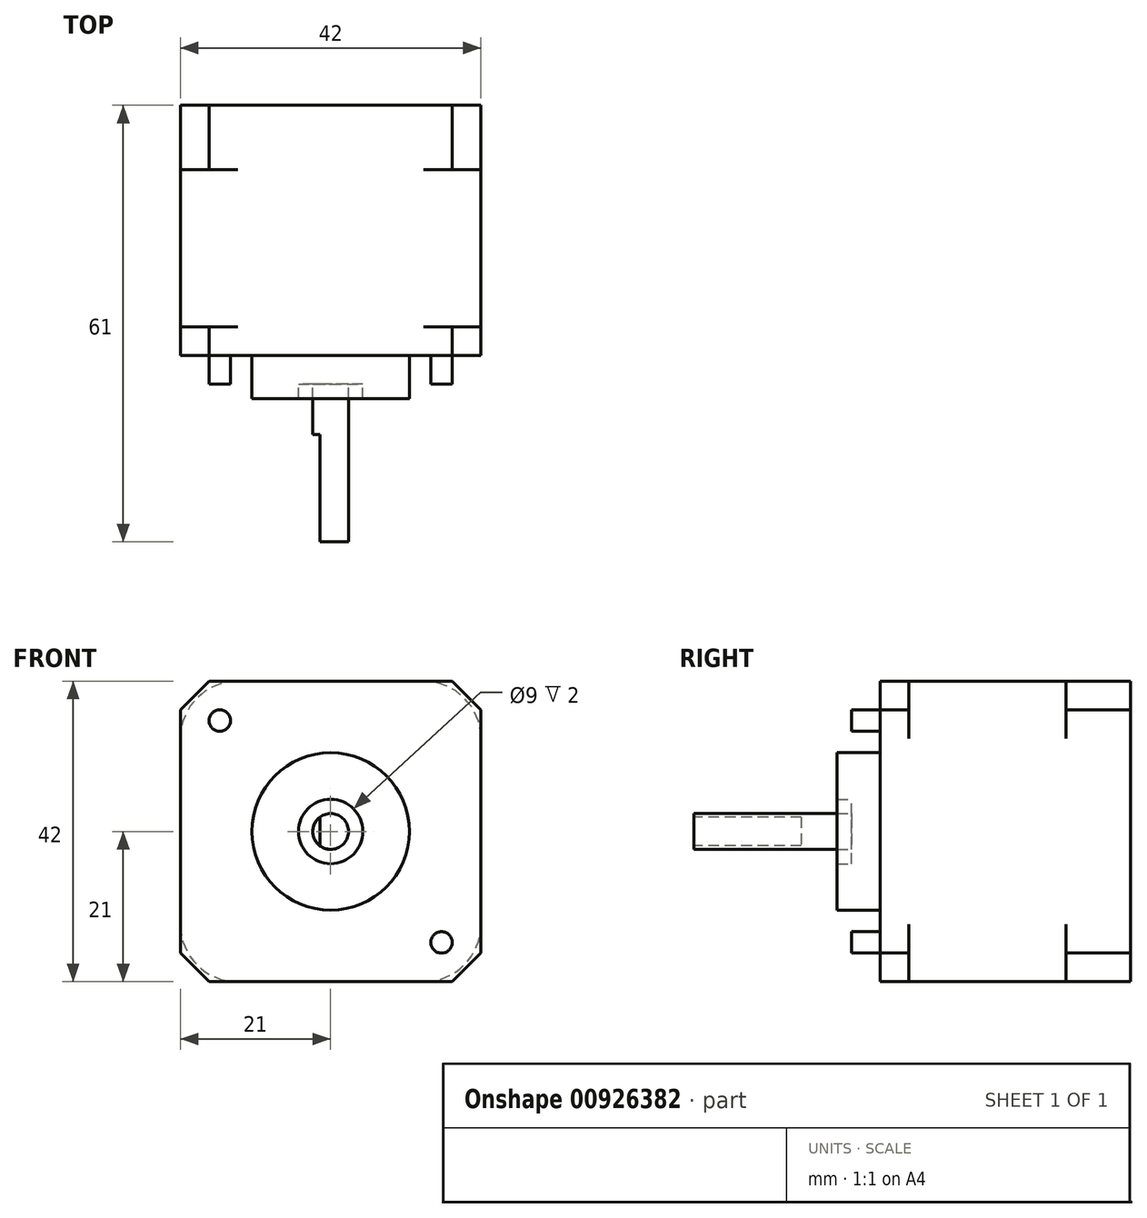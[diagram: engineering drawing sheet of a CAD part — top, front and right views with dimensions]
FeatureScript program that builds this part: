
annotation { "Feature Type Name" : "Feature", "Feature Type Description" : "" }
export const myFeature = defineFeature(function(context is Context, id is Id, definition is map)
    precondition{}
    {
        {
            var Q0;
            Q0=qCreatedBy(makeId("Front.planeOp"),FACE);
            var sketch = newSketch(context, id + "F0", { "sketchPlane" : qUnion([Q0])});
            skLineSegment(sketch, "E0.bottom", {"start": v(0, 0) * mm, "end": v(42, 0) * mm});
            skLineSegment(sketch, "E0.top", {"start": v(0, 42) * mm, "end": v(42, 42) * mm});
            skLineSegment(sketch, "E0.left", {"start": v(0, 0) * mm, "end": v(0, 42) * mm});
            skLineSegment(sketch, "E0.right", {"start": v(42, 0) * mm, "end": v(42, 42) * mm});
            skSolve(sketch);
        }
        {
            var Q0;
            Q0 = qSketchRegion(id + "F0", true);
            extrude(context, id + "F1", {"entities" : qUnion([Q0]), "depth" : 8 * mm, "offsetDistance" : 25 * mm});
        }
        {
            var Q0;
            Q0=makeQuery(id+"F1.opExtrude","CAP_FACE",FACE,{"disambiguationData":[OSD([sQuery(id+"F0.wireOp",EDGE,"E0.bottom"),sQuery(id+"F0.wireOp",EDGE,"E0.top"),sQuery(id+"F0.wireOp",EDGE,"E0.left"),sQuery(id+"F0.wireOp",EDGE,"E0.right")])],"isStart":true});
            var sketch = newSketch(context, id + "F2", { "sketchPlane" : qUnion([Q0])});
            skLineSegment(sketch, "E1", {"start": v(0, 21) * mm, "end": v(-42, 21) * mm, "construction": true});
            skLineSegment(sketch, "E2", {"start": v(-21, 42) * mm, "end": v(-21, 0) * mm, "construction": true});
            skLineSegment(sketch, "E3", {"start": v(0, 21) * mm, "end": v(0, 34) * mm});
            skLineSegment(sketch, "E4", {"start": v(-8, 42) * mm, "end": v(-21, 42) * mm});
            skLineSegment(sketch, "E5.MirrorCS", {"start": v(0, 21) * mm, "end": v(0, 8) * mm});
            skLineSegment(sketch, "E6.MirrorCS", {"start": v(-8, 0) * mm, "end": v(-21, 0) * mm});
            skLineSegment(sketch, "E7.MirrorCS", {"start": v(-42, 21) * mm, "end": v(-42, 8) * mm});
            skLineSegment(sketch, "E8.MirrorCS", {"start": v(-34, 42) * mm, "end": v(-21, 42) * mm});
            skLineSegment(sketch, "E9.MirrorCS", {"start": v(-34, 0) * mm, "end": v(-21, 0) * mm});
            skLineSegment(sketch, "E10.MirrorCS", {"start": v(-42, 21) * mm, "end": v(-42, 34) * mm});
            skArc(sketch, "E11", {"start": v(0, 34) * mm, "mid": v(-2.34, 39.66) * mm, "end": v(-8, 42) * mm});
            skArc(sketch, "E12.MirrorCS", {"start": v(0, 8) * mm, "mid": v(-2.34, 2.34) * mm, "end": v(-8, 0) * mm});
            skArc(sketch, "E13.MirrorCS", {"start": v(-42, 34) * mm, "mid": v(-39.66, 39.66) * mm, "end": v(-34, 42) * mm});
            skArc(sketch, "E14.MirrorCS", {"start": v(-42, 8) * mm, "mid": v(-39.66, 2.34) * mm, "end": v(-34, 0) * mm});
            skSolve(sketch);
        }
        {
            var Q0;
            Q0 = qSketchRegion(id + "F2", true);
            extrude(context, id + "F3", {"entities" : qUnion([Q0]), "operationType" : NewBodyOperationType.ADD, "depth" : 22 * mm, "offsetDistance" : 25 * mm});
        }
        {
            var Q0;
            Q0=makeQuery(id+"F3.opExtrude","CAP_FACE",FACE,{"disambiguationData":[OSD([sQuery(id+"F2.wireOp",EDGE,"E3"),sQuery(id+"F2.wireOp",EDGE,"TS49GkIp-gIQR-fzWl-7jLC-N3Z3hN07Um4u"),sQuery(id+"F2.wireOp",EDGE,"E4"),sQuery(id+"F2.wireOp",EDGE,"E5.MirrorCS"),sQuery(id+"F2.wireOp",EDGE,"e7304309-2cf8-4616-bcc9-8bdb39e604d01.MirrorCS"),sQuery(id+"F2.wireOp",EDGE,"E6.MirrorCS"),sQuery(id+"F2.wireOp",EDGE,"E7.MirrorCS"),sQuery(id+"F2.wireOp",EDGE,"8c1482cd-ad9f-4f6b-a8f8-884175ea14cf1.MirrorCS"),sQuery(id+"F2.wireOp",EDGE,"E8.MirrorCS"),sQuery(id+"F2.wireOp",EDGE,"8c1482cd-ad9f-4f6b-a8f8-884175ea14cf3.MirrorCS"),sQuery(id+"F2.wireOp",EDGE,"E9.MirrorCS"),sQuery(id+"F2.wireOp",EDGE,"E10.MirrorCS")])],"isStart":false});
            var sketch = newSketch(context, id + "F4", { "sketchPlane" : qUnion([Q0])});
            skLineSegment(sketch, "E15.bottom", {"start": v(0, 0) * mm, "end": v(-42, 0) * mm});
            skLineSegment(sketch, "E15.top", {"start": v(0, 42) * mm, "end": v(-42, 42) * mm});
            skLineSegment(sketch, "E15.left", {"start": v(0, 0) * mm, "end": v(0, 42) * mm});
            skLineSegment(sketch, "E15.right", {"start": v(-42, 0) * mm, "end": v(-42, 42) * mm});
            skSolve(sketch);
        }
        {
            var Q0;
            Q0 = qSketchRegion(id + "F4", true);
            extrude(context, id + "F5", {"entities" : qUnion([Q0]), "operationType" : NewBodyOperationType.ADD, "depth" : 9 * mm, "offsetDistance" : 25 * mm});
        }
        {
            var Q0;
            Q0=makeQuery(id+"F1.opExtrude","CAP_FACE",FACE,{"disambiguationData":[OSD([sQuery(id+"F0.wireOp",EDGE,"E0.bottom"),sQuery(id+"F0.wireOp",EDGE,"E0.top"),sQuery(id+"F0.wireOp",EDGE,"E0.left"),sQuery(id+"F0.wireOp",EDGE,"E0.right")])],"isStart":false});
            var sketch = newSketch(context, id + "F6", { "sketchPlane" : qUnion([Q0])});
            skLineSegment(sketch, "E16", {"start": v(0, 21) * mm, "end": v(42, 21) * mm, "construction": true});
            skLineSegment(sketch, "E17", {"start": v(21, 0) * mm, "end": v(21, 42) * mm, "construction": true});
            skCircle(sketch, "E18", {"center": v(21, 21) * mm, "radius": 11 * mm});
            skCircle(sketch, "E19", {"center": v(21, 21) * mm, "radius": 4.5 * mm});
            skSolve(sketch);
        }
        {
            var Q0;
            Q0=makeQuery(id+"F6.imprint","IMPRINT",FACE,{"disambiguationData":[TD([[makeQuery(id+"F6.imprint","IMPRINT",EDGE,{"derivedFrom":sQuery(id+"F6.wireOp",EDGE,"E18")}),1.0]])]});
            extrude(context, id + "F7", {"entities" : qUnion([Q0]), "operationType" : NewBodyOperationType.ADD, "depth" : 2 * mm, "offsetDistance" : 25 * mm});
        }
        {
            var Q0;
            Q0=makeQuery(id+"F7.boolean.opBoolean","SPLIT",FACE,{"disambiguationData":[TD([makeQuery(id+"F7.opExtrude","SWEPT_FACE",FACE,{"disambiguationData":[OSD([sQuery(id+"F6.wireOp",EDGE,"E19")])]})])],"derivedFrom":makeQuery(id+"F1.opExtrude","CAP_FACE",FACE,{"disambiguationData":[OSD([sQuery(id+"F0.wireOp",EDGE,"E0.bottom"),sQuery(id+"F0.wireOp",EDGE,"E0.top"),sQuery(id+"F0.wireOp",EDGE,"E0.left"),sQuery(id+"F0.wireOp",EDGE,"E0.right")])],"isStart":false})});
            var sketch = newSketch(context, id + "F8", { "sketchPlane" : qUnion([Q0])});
            skCircle(sketch, "E20", {"center": v(21, 21) * mm, "radius": 2.5 * mm});
            skSolve(sketch);
        }
        {
            var Q0;
            Q0 = qSketchRegion(id + "F8", true);
            extrude(context, id + "F9", {"entities" : qUnion([Q0]), "operationType" : NewBodyOperationType.ADD, "depth" : 22 * mm, "offsetDistance" : 25 * mm});
        }
        {
            var Q0;
            Q0=makeQuery(id+"F9.opExtrude","CAP_FACE",FACE,{"disambiguationData":[OSD([sQuery(id+"F8.wireOp",EDGE,"E20")])],"isStart":false});
            var sketch = newSketch(context, id + "F10", { "sketchPlane" : qUnion([Q0])});
            skLineSegment(sketch, "E21.bottom", {"start": v(19.5, 23) * mm, "end": v(18.5, 23) * mm});
            skLineSegment(sketch, "E21.top", {"start": v(19.5, 19) * mm, "end": v(18.5, 19) * mm});
            skLineSegment(sketch, "E21.left", {"start": v(19.5, 23) * mm, "end": v(19.5, 19) * mm});
            skLineSegment(sketch, "E21.right", {"start": v(18.5, 23) * mm, "end": v(18.5, 19) * mm});
            skSolve(sketch);
        }
        {
            var Q0;
            {var subQ0=sQuery(id+"F10.wireOp",EDGE,"E21.left");Q0=makeQuery(id+"F10.imprint","IMPRINT",FACE,{"disambiguationData":[TD([[makeQuery(id+"F10.imprint","IMPRINT",EDGE,{"derivedFrom":subQ0}),-1.0]])]});}
            extrude(context, id + "F11", {"entities" : qUnion([Q0]), "operationType" : NewBodyOperationType.REMOVE, "oppositeDirection" : true, "depth" : 15 * mm, "offsetDistance" : 25 * mm});
        }
        {
            var Q0;
            {var subQ0=sQuery(id+"F0.wireOp",EDGE,"E0.top");var subQ1=sQuery(id+"F0.wireOp",EDGE,"E0.bottom");var subQ2=sQuery(id+"F0.wireOp",EDGE,"E0.left");var subQ3=sQuery(id+"F0.wireOp",EDGE,"E0.right");Q0=makeQuery(id+"F7.boolean.opBoolean","SPLIT",FACE,{"disambiguationData":[TD([makeQuery(id+"F1.opExtrude","SWEPT_FACE",FACE,{"disambiguationData":[OSD([subQ1])]})])],"derivedFrom":makeQuery(id+"F1.opExtrude","CAP_FACE",FACE,{"disambiguationData":[OSD([subQ1,subQ0,subQ2,subQ3])],"isStart":false})});}
            var sketch = newSketch(context, id + "F12", { "sketchPlane" : qUnion([Q0])});
            skCircle(sketch, "E22", {"center": v(5.5, 5.5) * mm, "radius": 1.5 * mm});
            skLineSegment(sketch, "E23", {"start": v(0, 21) * mm, "end": v(42, 21) * mm, "construction": true});
            skLineSegment(sketch, "E24", {"start": v(21, 0) * mm, "end": v(21, 42) * mm, "construction": true});
            skCircle(sketch, "E25.MirrorC", {"center": v(5.5, 36.5) * mm, "radius": 1.5 * mm});
            skCircle(sketch, "E26.MirrorC", {"center": v(36.5, 36.5) * mm, "radius": 1.5 * mm});
            skCircle(sketch, "E27.MirrorC", {"center": v(36.5, 5.5) * mm, "radius": 1.5 * mm});
            skSolve(sketch);
        }
        {
            var Q0;
            Q0=makeQuery(id+"F12.imprint","IMPRINT",FACE,{"disambiguationData":[TD([[makeQuery(id+"F12.imprint","IMPRINT",EDGE,{"derivedFrom":sQuery(id+"F12.wireOp",EDGE,"E22")}),1.0]])]});
            var Q1;
            Q1=makeQuery(id+"F12.imprint","IMPRINT",FACE,{"disambiguationData":[TD([[makeQuery(id+"F12.imprint","IMPRINT",EDGE,{"derivedFrom":sQuery(id+"F12.wireOp",EDGE,"E25.MirrorC")}),-1.0]])]});
            var Q2;
            Q2=makeQuery(id+"F12.imprint","IMPRINT",FACE,{"disambiguationData":[TD([[makeQuery(id+"F12.imprint","IMPRINT",EDGE,{"derivedFrom":sQuery(id+"F12.wireOp",EDGE,"E26.MirrorC")}),1.0]])]});
            var Q3;
            Q3=makeQuery(id+"F12.imprint","IMPRINT",FACE,{"disambiguationData":[TD([[makeQuery(id+"F12.imprint","IMPRINT",EDGE,{"derivedFrom":sQuery(id+"F12.wireOp",EDGE,"E27.MirrorC")}),-1.0]])]});
            extrude(context, id + "F13", {"entities" : qUnion([Q0, Q1, Q2, Q3]), "operationType" : NewBodyOperationType.REMOVE, "oppositeDirection" : true, "depth" : 4 * mm, "offsetDistance" : 25 * mm});
        }
        {
            var Q0;
            Q0=makeQuery(id+"F1.opExtrude","SWEPT_EDGE",EDGE,{"disambiguationData":[OSD([sQuery(id+"F0.wireOp",EDGE,"E0.top"),sQuery(id+"F0.wireOp",EDGE,"E0.left")])]});
            var Q1;
            Q1=makeQuery(id+"F5.opExtrude","SWEPT_EDGE",EDGE,{"disambiguationData":[OSD([sQuery(id+"F4.wireOp",EDGE,"E15.top"),sQuery(id+"F4.wireOp",EDGE,"E15.left")])]});
            var Q2;
            Q2=makeQuery(id+"F1.opExtrude","SWEPT_EDGE",EDGE,{"disambiguationData":[OSD([sQuery(id+"F0.wireOp",EDGE,"E0.top"),sQuery(id+"F0.wireOp",EDGE,"E0.right")])]});
            var Q3;
            Q3=makeQuery(id+"F5.opExtrude","SWEPT_EDGE",EDGE,{"disambiguationData":[OSD([sQuery(id+"F4.wireOp",EDGE,"E15.top"),sQuery(id+"F4.wireOp",EDGE,"E15.right")])]});
            var Q4;
            Q4=makeQuery(id+"F5.opExtrude","SWEPT_EDGE",EDGE,{"disambiguationData":[OSD([sQuery(id+"F4.wireOp",EDGE,"E15.bottom"),sQuery(id+"F4.wireOp",EDGE,"E15.right")])]});
            var Q5;
            Q5=makeQuery(id+"F1.opExtrude","SWEPT_EDGE",EDGE,{"disambiguationData":[OSD([sQuery(id+"F0.wireOp",EDGE,"E0.bottom"),sQuery(id+"F0.wireOp",EDGE,"E0.right")])]});
            var Q6;
            Q6=makeQuery(id+"F1.opExtrude","SWEPT_EDGE",EDGE,{"disambiguationData":[OSD([sQuery(id+"F0.wireOp",EDGE,"E0.bottom"),sQuery(id+"F0.wireOp",EDGE,"E0.left")])]});
            var Q7;
            Q7=makeQuery(id+"F5.opExtrude","SWEPT_EDGE",EDGE,{"disambiguationData":[OSD([sQuery(id+"F4.wireOp",EDGE,"E15.bottom"),sQuery(id+"F4.wireOp",EDGE,"E15.left")])]});
            chamfer(context, id + "F14", {"entities" : qUnion([Q0, Q1, Q2, Q3, Q4, Q5, Q6, Q7]), "width" : 4 * mm, "tangentPropagation" : true});
        }
    });
